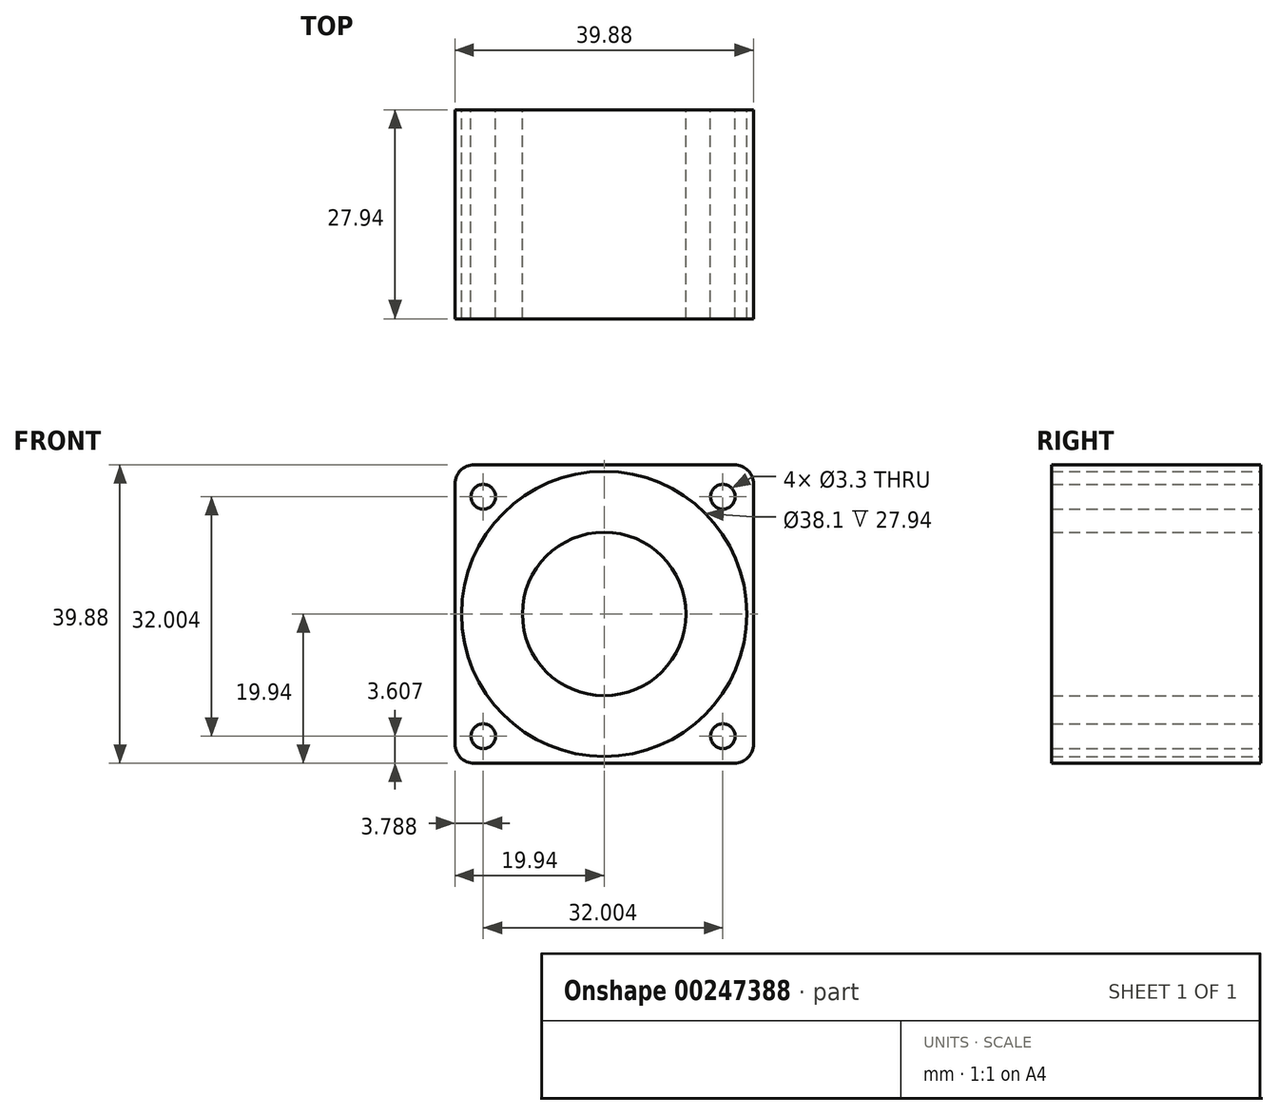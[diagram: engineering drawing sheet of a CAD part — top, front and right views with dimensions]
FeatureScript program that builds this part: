
annotation { "Feature Type Name" : "Feature", "Feature Type Description" : "" }
export const myFeature = defineFeature(function(context is Context, id is Id, definition is map)
    precondition{}
    {
        {
            var Q0;
            Q0=qCreatedBy(makeId("Front.planeOp"),FACE);
            var sketch = newSketch(context, id + "F0", { "sketchPlane" : qUnion([Q0])});
            skCircle(sketch, "E0", {"center": v(0, 0) * mm, "radius": 19.05 * mm});
            skLineSegment(sketch, "E1.bottom", {"start": v(19.94, -19.94) * mm, "end": v(-19.94, -19.94) * mm});
            skLineSegment(sketch, "E1.top", {"start": v(19.94, 19.94) * mm, "end": v(-19.94, 19.94) * mm});
            skLineSegment(sketch, "E1.left", {"start": v(19.94, -19.94) * mm, "end": v(19.94, 19.94) * mm});
            skLineSegment(sketch, "E1.right", {"start": v(-19.94, -19.94) * mm, "end": v(-19.94, 19.94) * mm});
            skCircle(sketch, "E2", {"center": v(0, 0) * mm, "radius": 10.92 * mm});
            skSolve(sketch);
        }
        {
            var Q0;
            Q0=makeQuery(id+"F0.imprint","IMPRINT",FACE,{"disambiguationData":[TD([[makeQuery(id+"F0.imprint","IMPRINT",EDGE,{"derivedFrom":sQuery(id+"F0.wireOp",EDGE,"E2")}),-1.0]])]});
            var sketch = newSketch(context, id + "F1", { "sketchPlane" : qUnion([Q0])});
            skPoint(sketch, "E3", {"position": v(-16.15, 15.67) * mm});
            skPoint(sketch, "E4", {"position": v(15.85, 15.67) * mm});
            skPoint(sketch, "E5", {"position": v(-16.15, -16.33) * mm});
            skPoint(sketch, "E6", {"position": v(15.85, -16.33) * mm});
            skCircle(sketch, "E7", {"center": v(-16.15, 15.67) * mm, "radius": 1.65 * mm});
            skCircle(sketch, "E8", {"center": v(15.85, 15.67) * mm, "radius": 1.65 * mm});
            skCircle(sketch, "E9", {"center": v(-16.15, -16.33) * mm, "radius": 1.65 * mm});
            skCircle(sketch, "E10", {"center": v(15.85, -16.33) * mm, "radius": 1.65 * mm});
            skSolve(sketch);
        }
        {
            var Q0;
            {var subQ0=sQuery(id+"F0.wireOp",EDGE,"E1.right");var subQ1=sQuery(id+"F0.wireOp",EDGE,"E0");var subQ2=makeQuery(id+"F0.imprint","INTERSECT",VERTEX,{"derivedFrom":[subQ1,subQ0]});Q0=makeQuery(id+"F0.imprint","IMPRINT",FACE,{"disambiguationData":[TD([[makeQuery(id+"F0.imprint","IMPRINT",EDGE,{"disambiguationData":[TD([[subQ2,-1.0]])],"derivedFrom":subQ1}),-1.0]])]});}
            var Q1;
            Q1=makeQuery(id+"F0.imprint","IMPRINT",FACE,{"disambiguationData":[TD([[makeQuery(id+"F0.imprint","IMPRINT",EDGE,{"derivedFrom":sQuery(id+"F0.wireOp",EDGE,"E2")}),1.0]])]});
            var Q2;
            {var subQ0=sQuery(id+"F0.wireOp",EDGE,"E1.left");var subQ1=sQuery(id+"F0.wireOp",EDGE,"E0");var subQ2=makeQuery(id+"F0.imprint","INTERSECT",VERTEX,{"derivedFrom":[subQ1,subQ0]});Q2=makeQuery(id+"F0.imprint","IMPRINT",FACE,{"disambiguationData":[TD([[makeQuery(id+"F0.imprint","IMPRINT",EDGE,{"disambiguationData":[TD([[subQ2,1.0]])],"derivedFrom":subQ1}),-1.0]])]});}
            var Q3;
            {var subQ0=sQuery(id+"F0.wireOp",EDGE,"E1.top");var subQ1=sQuery(id+"F0.wireOp",EDGE,"E0");var subQ2=makeQuery(id+"F0.imprint","INTERSECT",VERTEX,{"derivedFrom":[subQ1,subQ0]});Q3=makeQuery(id+"F0.imprint","IMPRINT",FACE,{"disambiguationData":[TD([[makeQuery(id+"F0.imprint","IMPRINT",EDGE,{"disambiguationData":[TD([[subQ2,1.0]])],"derivedFrom":subQ1}),-1.0]])]});}
            var Q4;
            {var subQ0=sQuery(id+"F0.wireOp",EDGE,"E1.top");var subQ1=sQuery(id+"F0.wireOp",EDGE,"E0");var subQ2=makeQuery(id+"F0.imprint","INTERSECT",VERTEX,{"derivedFrom":[subQ1,subQ0]});Q4=makeQuery(id+"F0.imprint","IMPRINT",FACE,{"disambiguationData":[TD([[makeQuery(id+"F0.imprint","IMPRINT",EDGE,{"disambiguationData":[TD([[subQ2,-1.0]])],"derivedFrom":subQ1}),-1.0]])]});}
            extrude(context, id + "F2", {"entities" : qUnion([Q0, Q1, Q2, Q3, Q4]), "depth" : 27.94 * mm});
        }
        {
            var Q0;
            Q0=sQuery(id+"F1.wireOp",VERTEX,"E6");
            var Q1;
            Q1=sQuery(id+"F1.wireOp",VERTEX,"E4");
            var Q2;
            Q2=sQuery(id+"F1.wireOp",VERTEX,"E5");
            var Q3;
            Q3=sQuery(id+"F1.wireOp",VERTEX,"E3");
            var Q4;
            Q4=makeQuery(id+"F2.opExtrude","SWEPT_BODY",BODY,{"disambiguationData":[OSD([sQuery(id+"F0.wireOp",EDGE,"E0"),sQuery(id+"F0.wireOp",EDGE,"E1.bottom"),sQuery(id+"F0.wireOp",EDGE,"E1.top"),sQuery(id+"F0.wireOp",EDGE,"E1.left"),sQuery(id+"F0.wireOp",EDGE,"E1.right")])]});
            hole(context, id + "F3", {"style" : HoleStyle.SIMPLE, "endStyle" : HoleEndStyle.THROUGH, "oppositeDirection" : true, "holeDiameter" : 3.3 * mm, "tappedDepth" : 12.7 * mm, "tapClearance" : 3, "locations" : qUnion([Q0, Q1, Q2, Q3]), "scope" : qUnion([Q4])});
        }
        {
            var Q0;
            Q0=makeQuery(id+"F2.opExtrude","SWEPT_EDGE",EDGE,{"disambiguationData":[OSD([sQuery(id+"F0.wireOp",EDGE,"E1.top"),sQuery(id+"F0.wireOp",EDGE,"E1.left")])]});
            var Q1;
            Q1=makeQuery(id+"F2.opExtrude","SWEPT_EDGE",EDGE,{"disambiguationData":[OSD([sQuery(id+"F0.wireOp",EDGE,"E1.top"),sQuery(id+"F0.wireOp",EDGE,"E1.right")])]});
            var Q2;
            Q2=makeQuery(id+"F2.opExtrude","SWEPT_EDGE",EDGE,{"disambiguationData":[OSD([sQuery(id+"F0.wireOp",EDGE,"E1.bottom"),sQuery(id+"F0.wireOp",EDGE,"E1.right")])]});
            var Q3;
            Q3=makeQuery(id+"F2.opExtrude","SWEPT_EDGE",EDGE,{"disambiguationData":[OSD([sQuery(id+"F0.wireOp",EDGE,"E1.bottom"),sQuery(id+"F0.wireOp",EDGE,"E1.left")])]});
            fillet(context, id + "F4", {"entities" : qUnion([Q0, Q1, Q2, Q3]), "radius" : 2.54 * mm, "tangentPropagation" : true, "allowEdgeOverflow" : false});
        }
    });
